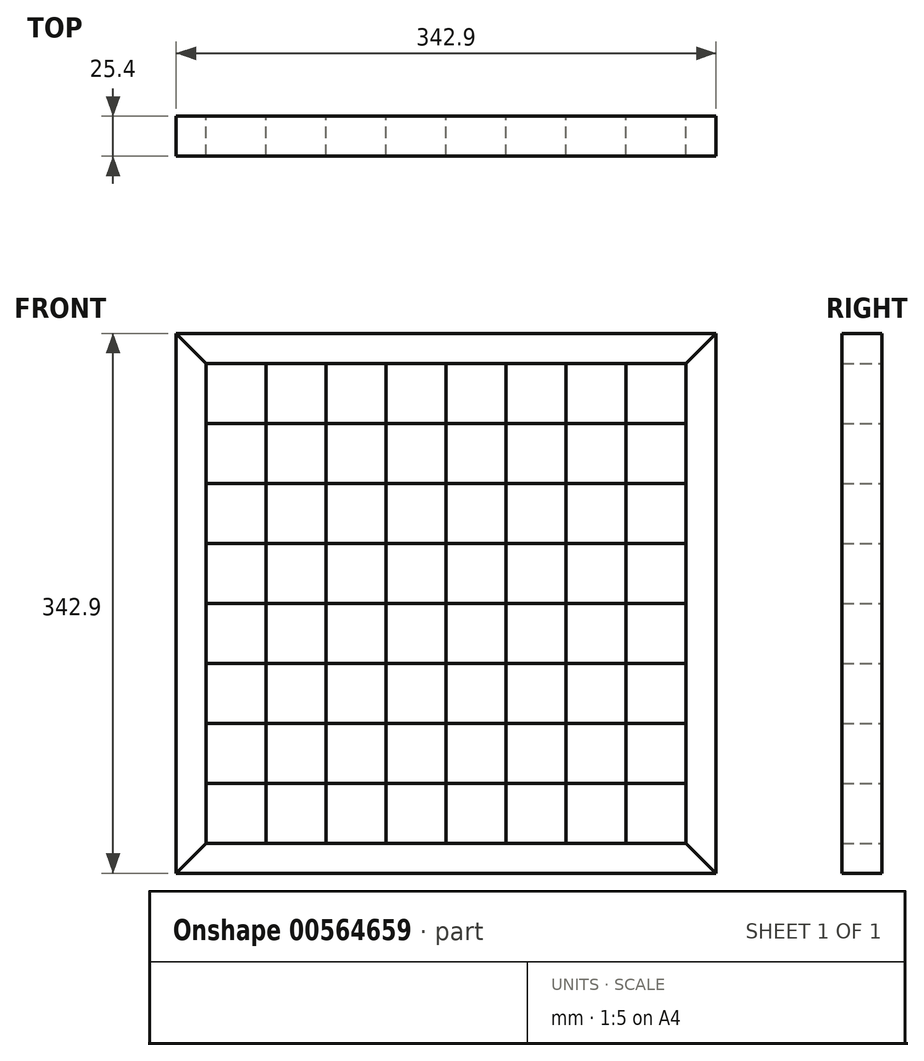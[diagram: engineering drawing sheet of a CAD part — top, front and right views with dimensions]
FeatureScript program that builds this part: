
annotation { "Feature Type Name" : "Feature", "Feature Type Description" : "" }
export const myFeature = defineFeature(function(context is Context, id is Id, definition is map)
    precondition{}
    {
        {
            var Q0;
            Q0=qCreatedBy(makeId("Front.planeOp"),FACE);
            var sketch = newSketch(context, id + "F0", { "sketchPlane" : qUnion([Q0])});
            skLineSegment(sketch, "E0.bottom", {"start": v(171.45, -171.45) * mm, "end": v(-171.45, -171.45) * mm});
            skLineSegment(sketch, "E0.top", {"start": v(171.45, 171.45) * mm, "end": v(-171.45, 171.45) * mm});
            skLineSegment(sketch, "E0.left", {"start": v(171.45, -171.45) * mm, "end": v(171.45, 171.45) * mm});
            skLineSegment(sketch, "E0.right", {"start": v(-171.45, -171.45) * mm, "end": v(-171.45, 171.45) * mm});
            skPoint(sketch, "E0.middle", {"position": v(0, 0) * mm});
            skLineSegment(sketch, "E1.bottom", {"start": v(152.4, -152.4) * mm, "end": v(-152.4, -152.4) * mm});
            skLineSegment(sketch, "E1.top", {"start": v(152.4, 152.4) * mm, "end": v(-152.4, 152.4) * mm});
            skLineSegment(sketch, "E1.left", {"start": v(152.4, -152.4) * mm, "end": v(152.4, 152.4) * mm});
            skLineSegment(sketch, "E1.right", {"start": v(-152.4, -152.4) * mm, "end": v(-152.4, 152.4) * mm});
            skLineSegment(sketch, "E2.0", {"start": v(152.4, 114.3) * mm, "end": v(-152.4, 114.3) * mm});
            skLineSegment(sketch, "E3.0", {"start": v(152.4, 76.2) * mm, "end": v(-152.4, 76.2) * mm});
            skLineSegment(sketch, "E4.0", {"start": v(152.4, 38.1) * mm, "end": v(-152.4, 38.1) * mm});
            skLineSegment(sketch, "E5.0", {"start": v(152.4, 0) * mm, "end": v(-152.4, 0) * mm});
            skLineSegment(sketch, "E6.0", {"start": v(152.4, -38.1) * mm, "end": v(-152.4, -38.1) * mm});
            skLineSegment(sketch, "E7.0", {"start": v(152.4, -76.2) * mm, "end": v(-152.4, -76.2) * mm});
            skLineSegment(sketch, "E8.0", {"start": v(152.4, -114.3) * mm, "end": v(-152.4, -114.3) * mm});
            skLineSegment(sketch, "E9.0", {"start": v(-114.3, -152.4) * mm, "end": v(-114.3, 152.4) * mm});
            skLineSegment(sketch, "E10.0", {"start": v(-76.2, -152.4) * mm, "end": v(-76.2, 152.4) * mm});
            skLineSegment(sketch, "E11.0", {"start": v(-38.1, -152.4) * mm, "end": v(-38.1, 152.4) * mm});
            skLineSegment(sketch, "E12.0", {"start": v(0, -152.4) * mm, "end": v(0, 152.4) * mm});
            skLineSegment(sketch, "E13.0", {"start": v(38.1, -152.4) * mm, "end": v(38.1, 152.4) * mm});
            skLineSegment(sketch, "E14.0", {"start": v(76.2, -152.4) * mm, "end": v(76.2, 152.4) * mm});
            skLineSegment(sketch, "E15.0", {"start": v(114.3, -152.4) * mm, "end": v(114.3, 152.4) * mm});
            skLineSegment(sketch, "E16", {"start": v(-152.4, 152.4) * mm, "end": v(-171.45, 171.45) * mm});
            skLineSegment(sketch, "E17", {"start": v(171.45, 171.45) * mm, "end": v(152.4, 152.4) * mm});
            skLineSegment(sketch, "E18", {"start": v(152.4, -152.4) * mm, "end": v(171.45, -171.45) * mm});
            skLineSegment(sketch, "E19", {"start": v(-152.4, -152.4) * mm, "end": v(-171.45, -171.45) * mm});
            skSolve(sketch);
        }
        {
            var Q0;
            Q0=makeQuery(id+"F0.imprint","IMPRINT",FACE,{"disambiguationData":[TD([[makeQuery(id+"F0.imprint","IMPRINT",EDGE,{"derivedFrom":sQuery(id+"F0.wireOp",EDGE,"E0.top")}),1.0]])]});
            extrude(context, id + "F1", {"entities" : qUnion([Q0]), "depth" : 25.4 * mm, "offsetDistance" : 25.4 * mm});
        }
        {
            var Q0;
            Q0=makeQuery(id+"F0.imprint","IMPRINT",FACE,{"disambiguationData":[TD([[makeQuery(id+"F0.imprint","IMPRINT",EDGE,{"derivedFrom":sQuery(id+"F0.wireOp",EDGE,"E0.right")}),-1.0]])]});
            extrude(context, id + "F2", {"entities" : qUnion([Q0]), "depth" : 25.4 * mm, "offsetDistance" : 25.4 * mm});
        }
        {
            var Q0;
            Q0=makeQuery(id+"F0.imprint","IMPRINT",FACE,{"disambiguationData":[TD([[makeQuery(id+"F0.imprint","IMPRINT",EDGE,{"derivedFrom":sQuery(id+"F0.wireOp",EDGE,"E0.left")}),1.0]])]});
            extrude(context, id + "F3", {"entities" : qUnion([Q0]), "depth" : 25.4 * mm, "offsetDistance" : 25.4 * mm});
        }
        {
            var Q0;
            Q0=makeQuery(id+"F0.imprint","IMPRINT",FACE,{"disambiguationData":[TD([[makeQuery(id+"F0.imprint","IMPRINT",EDGE,{"derivedFrom":sQuery(id+"F0.wireOp",EDGE,"E0.bottom")}),-1.0]])]});
            extrude(context, id + "F4", {"entities" : qUnion([Q0]), "depth" : 25.4 * mm, "offsetDistance" : 25.4 * mm});
        }
        {
            var Q0;
            {var subQ0=sQuery(id+"F0.wireOp",EDGE,"E1.right");var subQ5=sQuery(id+"F0.wireOp",EDGE,"E2.0");var subQ7=makeQuery(id+"F0.imprint","INTERSECT",VERTEX,{"derivedFrom":[subQ0,subQ5]});Q0=makeQuery(id+"F0.imprint","IMPRINT",FACE,{"disambiguationData":[TD([[makeQuery(id+"F0.imprint","IMPRINT",EDGE,{"disambiguationData":[TD([[subQ7,1.0]])],"derivedFrom":subQ5}),-1.0]])]});}
            extrude(context, id + "F5", {"entities" : qUnion([Q0]), "depth" : 25.4 * mm, "offsetDistance" : 25.4 * mm});
        }
        {
            var Q0;
            {var subQ0=sQuery(id+"F0.wireOp",EDGE,"E2.0");var subQ1=sQuery(id+"F0.wireOp",EDGE,"E1.right");var subQ2=makeQuery(id+"F0.imprint","INTERSECT",VERTEX,{"derivedFrom":[subQ1,subQ0]});Q0=makeQuery(id+"F0.imprint","IMPRINT",FACE,{"disambiguationData":[TD([[makeQuery(id+"F0.imprint","IMPRINT",EDGE,{"disambiguationData":[TD([[subQ2,1.0]])],"derivedFrom":subQ1}),-1.0]])]});}
            extrude(context, id + "F6", {"entities" : qUnion([Q0]), "depth" : 25.4 * mm, "offsetDistance" : 25.4 * mm});
        }
        {
            var Q0;
            {var subQ0=sQuery(id+"F0.wireOp",EDGE,"E3.0");var subQ1=sQuery(id+"F0.wireOp",EDGE,"E1.right");var subQ2=makeQuery(id+"F0.imprint","INTERSECT",VERTEX,{"derivedFrom":[subQ1,subQ0]});Q0=makeQuery(id+"F0.imprint","IMPRINT",FACE,{"disambiguationData":[TD([[makeQuery(id+"F0.imprint","IMPRINT",EDGE,{"disambiguationData":[TD([[subQ2,1.0]])],"derivedFrom":subQ1}),-1.0]])]});}
            extrude(context, id + "F7", {"entities" : qUnion([Q0]), "depth" : 25.4 * mm, "offsetDistance" : 25.4 * mm});
        }
        {
            var Q0;
            {var subQ0=sQuery(id+"F0.wireOp",EDGE,"E4.0");var subQ1=sQuery(id+"F0.wireOp",EDGE,"E1.right");var subQ2=makeQuery(id+"F0.imprint","INTERSECT",VERTEX,{"derivedFrom":[subQ1,subQ0]});Q0=makeQuery(id+"F0.imprint","IMPRINT",FACE,{"disambiguationData":[TD([[makeQuery(id+"F0.imprint","IMPRINT",EDGE,{"disambiguationData":[TD([[subQ2,1.0]])],"derivedFrom":subQ1}),-1.0]])]});}
            extrude(context, id + "F8", {"entities" : qUnion([Q0]), "depth" : 25.4 * mm, "offsetDistance" : 25.4 * mm});
        }
        {
            var Q0;
            {var subQ0=sQuery(id+"F0.wireOp",EDGE,"E5.0");var subQ1=sQuery(id+"F0.wireOp",EDGE,"E1.right");var subQ2=makeQuery(id+"F0.imprint","INTERSECT",VERTEX,{"derivedFrom":[subQ1,subQ0]});Q0=makeQuery(id+"F0.imprint","IMPRINT",FACE,{"disambiguationData":[TD([[makeQuery(id+"F0.imprint","IMPRINT",EDGE,{"disambiguationData":[TD([[subQ2,1.0]])],"derivedFrom":subQ1}),-1.0]])]});}
            extrude(context, id + "F9", {"entities" : qUnion([Q0]), "depth" : 25.4 * mm, "offsetDistance" : 25.4 * mm});
        }
        {
            var Q0;
            {var subQ0=sQuery(id+"F0.wireOp",EDGE,"E6.0");var subQ1=sQuery(id+"F0.wireOp",EDGE,"E1.right");var subQ2=makeQuery(id+"F0.imprint","INTERSECT",VERTEX,{"derivedFrom":[subQ1,subQ0]});Q0=makeQuery(id+"F0.imprint","IMPRINT",FACE,{"disambiguationData":[TD([[makeQuery(id+"F0.imprint","IMPRINT",EDGE,{"disambiguationData":[TD([[subQ2,1.0]])],"derivedFrom":subQ1}),-1.0]])]});}
            extrude(context, id + "F10", {"entities" : qUnion([Q0]), "depth" : 25.4 * mm, "offsetDistance" : 25.4 * mm});
        }
        {
            var Q0;
            {var subQ0=sQuery(id+"F0.wireOp",EDGE,"E7.0");var subQ1=sQuery(id+"F0.wireOp",EDGE,"E1.right");var subQ2=makeQuery(id+"F0.imprint","INTERSECT",VERTEX,{"derivedFrom":[subQ1,subQ0]});Q0=makeQuery(id+"F0.imprint","IMPRINT",FACE,{"disambiguationData":[TD([[makeQuery(id+"F0.imprint","IMPRINT",EDGE,{"disambiguationData":[TD([[subQ2,1.0]])],"derivedFrom":subQ1}),-1.0]])]});}
            extrude(context, id + "F11", {"entities" : qUnion([Q0]), "depth" : 25.4 * mm, "offsetDistance" : 25.4 * mm});
        }
        {
            var Q0;
            {var subQ0=sQuery(id+"F0.wireOp",EDGE,"E1.right");var subQ5=sQuery(id+"F0.wireOp",EDGE,"E8.0");var subQ6=makeQuery(id+"F0.imprint","INTERSECT",VERTEX,{"derivedFrom":[subQ0,subQ5]});Q0=makeQuery(id+"F0.imprint","IMPRINT",FACE,{"disambiguationData":[TD([[makeQuery(id+"F0.imprint","IMPRINT",EDGE,{"disambiguationData":[TD([[subQ6,1.0]])],"derivedFrom":subQ5}),1.0]])]});}
            extrude(context, id + "F12", {"entities" : qUnion([Q0]), "depth" : 25.4 * mm, "offsetDistance" : 25.4 * mm});
        }
        {
            var Q0;
            {var subQ0=sQuery(id+"F0.wireOp",EDGE,"E9.0");var subQ1=sQuery(id+"F0.wireOp",EDGE,"E1.top");var subQ2=makeQuery(id+"F0.imprint","INTERSECT",VERTEX,{"derivedFrom":[subQ1,subQ0]});Q0=makeQuery(id+"F0.imprint","IMPRINT",FACE,{"disambiguationData":[TD([[makeQuery(id+"F0.imprint","IMPRINT",EDGE,{"disambiguationData":[TD([[subQ2,1.0]])],"derivedFrom":subQ1}),1.0]])]});}
            extrude(context, id + "F13", {"entities" : qUnion([Q0]), "depth" : 25.4 * mm, "offsetDistance" : 25.4 * mm});
        }
        {
            var Q0;
            {var subQ0=sQuery(id+"F0.wireOp",EDGE,"E10.0");var subQ1=sQuery(id+"F0.wireOp",EDGE,"E1.top");var subQ2=makeQuery(id+"F0.imprint","INTERSECT",VERTEX,{"derivedFrom":[subQ1,subQ0]});Q0=makeQuery(id+"F0.imprint","IMPRINT",FACE,{"disambiguationData":[TD([[makeQuery(id+"F0.imprint","IMPRINT",EDGE,{"disambiguationData":[TD([[subQ2,1.0]])],"derivedFrom":subQ1}),1.0]])]});}
            extrude(context, id + "F14", {"entities" : qUnion([Q0]), "depth" : 25.4 * mm, "offsetDistance" : 25.4 * mm});
        }
        {
            var Q0;
            {var subQ0=sQuery(id+"F0.wireOp",EDGE,"E11.0");var subQ1=sQuery(id+"F0.wireOp",EDGE,"E1.top");var subQ2=makeQuery(id+"F0.imprint","INTERSECT",VERTEX,{"derivedFrom":[subQ1,subQ0]});Q0=makeQuery(id+"F0.imprint","IMPRINT",FACE,{"disambiguationData":[TD([[makeQuery(id+"F0.imprint","IMPRINT",EDGE,{"disambiguationData":[TD([[subQ2,1.0]])],"derivedFrom":subQ1}),1.0]])]});}
            extrude(context, id + "F15", {"entities" : qUnion([Q0]), "depth" : 25.4 * mm, "offsetDistance" : 25.4 * mm});
        }
        {
            var Q0;
            {var subQ0=sQuery(id+"F0.wireOp",EDGE,"E12.0");var subQ1=sQuery(id+"F0.wireOp",EDGE,"E1.top");var subQ2=makeQuery(id+"F0.imprint","INTERSECT",VERTEX,{"derivedFrom":[subQ1,subQ0]});Q0=makeQuery(id+"F0.imprint","IMPRINT",FACE,{"disambiguationData":[TD([[makeQuery(id+"F0.imprint","IMPRINT",EDGE,{"disambiguationData":[TD([[subQ2,1.0]])],"derivedFrom":subQ1}),1.0]])]});}
            extrude(context, id + "F16", {"entities" : qUnion([Q0]), "depth" : 25.4 * mm, "offsetDistance" : 25.4 * mm});
        }
        {
            var Q0;
            {var subQ0=sQuery(id+"F0.wireOp",EDGE,"E13.0");var subQ1=sQuery(id+"F0.wireOp",EDGE,"E1.top");var subQ2=makeQuery(id+"F0.imprint","INTERSECT",VERTEX,{"derivedFrom":[subQ1,subQ0]});Q0=makeQuery(id+"F0.imprint","IMPRINT",FACE,{"disambiguationData":[TD([[makeQuery(id+"F0.imprint","IMPRINT",EDGE,{"disambiguationData":[TD([[subQ2,1.0]])],"derivedFrom":subQ1}),1.0]])]});}
            extrude(context, id + "F17", {"entities" : qUnion([Q0]), "depth" : 25.4 * mm, "offsetDistance" : 25.4 * mm});
        }
        {
            var Q0;
            {var subQ0=sQuery(id+"F0.wireOp",EDGE,"E14.0");var subQ1=sQuery(id+"F0.wireOp",EDGE,"E1.top");var subQ2=makeQuery(id+"F0.imprint","INTERSECT",VERTEX,{"derivedFrom":[subQ1,subQ0]});Q0=makeQuery(id+"F0.imprint","IMPRINT",FACE,{"disambiguationData":[TD([[makeQuery(id+"F0.imprint","IMPRINT",EDGE,{"disambiguationData":[TD([[subQ2,1.0]])],"derivedFrom":subQ1}),1.0]])]});}
            extrude(context, id + "F18", {"entities" : qUnion([Q0]), "depth" : 25.4 * mm, "offsetDistance" : 25.4 * mm});
        }
        {
            var Q0;
            {var subQ0=sQuery(id+"F0.wireOp",EDGE,"E1.left");var subQ5=sQuery(id+"F0.wireOp",EDGE,"E2.0");var subQ6=makeQuery(id+"F0.imprint","INTERSECT",VERTEX,{"derivedFrom":[subQ0,subQ5]});Q0=makeQuery(id+"F0.imprint","IMPRINT",FACE,{"disambiguationData":[TD([[makeQuery(id+"F0.imprint","IMPRINT",EDGE,{"disambiguationData":[TD([[subQ6,-1.0]])],"derivedFrom":subQ5}),-1.0]])]});}
            extrude(context, id + "F19", {"entities" : qUnion([Q0]), "depth" : 25.4 * mm, "offsetDistance" : 25.4 * mm});
        }
        {
            var Q0;
            {var subQ0=sQuery(id+"F0.wireOp",EDGE,"E10.0");var subQ1=sQuery(id+"F0.wireOp",EDGE,"E2.0");var subQ2=makeQuery(id+"F0.imprint","INTERSECT",VERTEX,{"derivedFrom":[subQ1,subQ0]});Q0=makeQuery(id+"F0.imprint","IMPRINT",FACE,{"disambiguationData":[TD([[makeQuery(id+"F0.imprint","IMPRINT",EDGE,{"disambiguationData":[TD([[subQ2,-1.0]])],"derivedFrom":subQ1}),1.0]])]});}
            var Q1;
            {var subQ0=sQuery(id+"F0.wireOp",EDGE,"E11.0");var subQ1=sQuery(id+"F0.wireOp",EDGE,"E3.0");var subQ2=makeQuery(id+"F0.imprint","INTERSECT",VERTEX,{"derivedFrom":[subQ1,subQ0]});Q1=makeQuery(id+"F0.imprint","IMPRINT",FACE,{"disambiguationData":[TD([[makeQuery(id+"F0.imprint","IMPRINT",EDGE,{"disambiguationData":[TD([[subQ2,-1.0]])],"derivedFrom":subQ1}),1.0]])]});}
            var Q2;
            {var subQ0=sQuery(id+"F0.wireOp",EDGE,"E12.0");var subQ1=sQuery(id+"F0.wireOp",EDGE,"E4.0");var subQ2=makeQuery(id+"F0.imprint","INTERSECT",VERTEX,{"derivedFrom":[subQ1,subQ0]});Q2=makeQuery(id+"F0.imprint","IMPRINT",FACE,{"disambiguationData":[TD([[makeQuery(id+"F0.imprint","IMPRINT",EDGE,{"disambiguationData":[TD([[subQ2,-1.0]])],"derivedFrom":subQ1}),1.0]])]});}
            var Q3;
            {var subQ0=sQuery(id+"F0.wireOp",EDGE,"E13.0");var subQ1=sQuery(id+"F0.wireOp",EDGE,"E5.0");var subQ2=makeQuery(id+"F0.imprint","INTERSECT",VERTEX,{"derivedFrom":[subQ1,subQ0]});Q3=makeQuery(id+"F0.imprint","IMPRINT",FACE,{"disambiguationData":[TD([[makeQuery(id+"F0.imprint","IMPRINT",EDGE,{"disambiguationData":[TD([[subQ2,-1.0]])],"derivedFrom":subQ1}),1.0]])]});}
            extrude(context, id + "F20", {"entities" : qUnion([Q0, Q1, Q2, Q3]), "depth" : 25.4 * mm, "offsetDistance" : 25.4 * mm});
        }
        {
            var Q0;
            {var subQ0=sQuery(id+"F0.wireOp",EDGE,"E14.0");var subQ1=sQuery(id+"F0.wireOp",EDGE,"E6.0");var subQ2=makeQuery(id+"F0.imprint","INTERSECT",VERTEX,{"derivedFrom":[subQ1,subQ0]});Q0=makeQuery(id+"F0.imprint","IMPRINT",FACE,{"disambiguationData":[TD([[makeQuery(id+"F0.imprint","IMPRINT",EDGE,{"disambiguationData":[TD([[subQ2,-1.0]])],"derivedFrom":subQ1}),1.0]])]});}
            var Q1;
            {var subQ0=sQuery(id+"F0.wireOp",EDGE,"E15.0");var subQ1=sQuery(id+"F0.wireOp",EDGE,"E7.0");var subQ2=makeQuery(id+"F0.imprint","INTERSECT",VERTEX,{"derivedFrom":[subQ1,subQ0]});Q1=makeQuery(id+"F0.imprint","IMPRINT",FACE,{"disambiguationData":[TD([[makeQuery(id+"F0.imprint","IMPRINT",EDGE,{"disambiguationData":[TD([[subQ2,-1.0]])],"derivedFrom":subQ1}),1.0]])]});}
            var Q2;
            {var subQ0=sQuery(id+"F0.wireOp",EDGE,"E1.left");var subQ5=sQuery(id+"F0.wireOp",EDGE,"E8.0");var subQ6=makeQuery(id+"F0.imprint","INTERSECT",VERTEX,{"derivedFrom":[subQ0,subQ5]});Q2=makeQuery(id+"F0.imprint","IMPRINT",FACE,{"disambiguationData":[TD([[makeQuery(id+"F0.imprint","IMPRINT",EDGE,{"disambiguationData":[TD([[subQ6,-1.0]])],"derivedFrom":subQ5}),1.0]])]});}
            extrude(context, id + "F21", {"entities" : qUnion([Q0, Q1, Q2]), "depth" : 25.4 * mm, "offsetDistance" : 25.4 * mm});
        }
        {
            var Q0;
            {var subQ0=sQuery(id+"F0.wireOp",EDGE,"E10.0");var subQ1=sQuery(id+"F0.wireOp",EDGE,"E3.0");var subQ2=makeQuery(id+"F0.imprint","INTERSECT",VERTEX,{"derivedFrom":[subQ1,subQ0]});Q0=makeQuery(id+"F0.imprint","IMPRINT",FACE,{"disambiguationData":[TD([[makeQuery(id+"F0.imprint","IMPRINT",EDGE,{"disambiguationData":[TD([[subQ2,-1.0]])],"derivedFrom":subQ1}),1.0]])]});}
            var Q1;
            {var subQ0=sQuery(id+"F0.wireOp",EDGE,"E11.0");var subQ1=sQuery(id+"F0.wireOp",EDGE,"E4.0");var subQ2=makeQuery(id+"F0.imprint","INTERSECT",VERTEX,{"derivedFrom":[subQ1,subQ0]});Q1=makeQuery(id+"F0.imprint","IMPRINT",FACE,{"disambiguationData":[TD([[makeQuery(id+"F0.imprint","IMPRINT",EDGE,{"disambiguationData":[TD([[subQ2,-1.0]])],"derivedFrom":subQ1}),1.0]])]});}
            var Q2;
            {var subQ0=sQuery(id+"F0.wireOp",EDGE,"E12.0");var subQ1=sQuery(id+"F0.wireOp",EDGE,"E5.0");var subQ2=makeQuery(id+"F0.imprint","INTERSECT",VERTEX,{"derivedFrom":[subQ1,subQ0]});Q2=makeQuery(id+"F0.imprint","IMPRINT",FACE,{"disambiguationData":[TD([[makeQuery(id+"F0.imprint","IMPRINT",EDGE,{"disambiguationData":[TD([[subQ2,-1.0]])],"derivedFrom":subQ1}),1.0]])]});}
            var Q3;
            {var subQ0=sQuery(id+"F0.wireOp",EDGE,"E13.0");var subQ1=sQuery(id+"F0.wireOp",EDGE,"E6.0");var subQ2=makeQuery(id+"F0.imprint","INTERSECT",VERTEX,{"derivedFrom":[subQ1,subQ0]});Q3=makeQuery(id+"F0.imprint","IMPRINT",FACE,{"disambiguationData":[TD([[makeQuery(id+"F0.imprint","IMPRINT",EDGE,{"disambiguationData":[TD([[subQ2,-1.0]])],"derivedFrom":subQ1}),1.0]])]});}
            var Q4;
            {var subQ0=sQuery(id+"F0.wireOp",EDGE,"E14.0");var subQ1=sQuery(id+"F0.wireOp",EDGE,"E7.0");var subQ2=makeQuery(id+"F0.imprint","INTERSECT",VERTEX,{"derivedFrom":[subQ1,subQ0]});Q4=makeQuery(id+"F0.imprint","IMPRINT",FACE,{"disambiguationData":[TD([[makeQuery(id+"F0.imprint","IMPRINT",EDGE,{"disambiguationData":[TD([[subQ2,-1.0]])],"derivedFrom":subQ1}),1.0]])]});}
            var Q5;
            {var subQ0=sQuery(id+"F0.wireOp",EDGE,"E14.0");var subQ1=sQuery(id+"F0.wireOp",EDGE,"E1.bottom");var subQ2=makeQuery(id+"F0.imprint","INTERSECT",VERTEX,{"derivedFrom":[subQ1,subQ0]});Q5=makeQuery(id+"F0.imprint","IMPRINT",FACE,{"disambiguationData":[TD([[makeQuery(id+"F0.imprint","IMPRINT",EDGE,{"disambiguationData":[TD([[subQ2,1.0]])],"derivedFrom":subQ1}),-1.0]])]});}
            extrude(context, id + "F22", {"entities" : qUnion([Q0, Q1, Q2, Q3, Q4, Q5]), "depth" : 25.4 * mm, "offsetDistance" : 25.4 * mm});
        }
        {
            var Q0;
            {var subQ0=sQuery(id+"F0.wireOp",EDGE,"E10.0");var subQ1=sQuery(id+"F0.wireOp",EDGE,"E4.0");var subQ2=makeQuery(id+"F0.imprint","INTERSECT",VERTEX,{"derivedFrom":[subQ1,subQ0]});Q0=makeQuery(id+"F0.imprint","IMPRINT",FACE,{"disambiguationData":[TD([[makeQuery(id+"F0.imprint","IMPRINT",EDGE,{"disambiguationData":[TD([[subQ2,-1.0]])],"derivedFrom":subQ1}),1.0]])]});}
            var Q1;
            {var subQ0=sQuery(id+"F0.wireOp",EDGE,"E11.0");var subQ1=sQuery(id+"F0.wireOp",EDGE,"E5.0");var subQ2=makeQuery(id+"F0.imprint","INTERSECT",VERTEX,{"derivedFrom":[subQ1,subQ0]});Q1=makeQuery(id+"F0.imprint","IMPRINT",FACE,{"disambiguationData":[TD([[makeQuery(id+"F0.imprint","IMPRINT",EDGE,{"disambiguationData":[TD([[subQ2,-1.0]])],"derivedFrom":subQ1}),1.0]])]});}
            var Q2;
            {var subQ0=sQuery(id+"F0.wireOp",EDGE,"E12.0");var subQ1=sQuery(id+"F0.wireOp",EDGE,"E6.0");var subQ2=makeQuery(id+"F0.imprint","INTERSECT",VERTEX,{"derivedFrom":[subQ1,subQ0]});Q2=makeQuery(id+"F0.imprint","IMPRINT",FACE,{"disambiguationData":[TD([[makeQuery(id+"F0.imprint","IMPRINT",EDGE,{"disambiguationData":[TD([[subQ2,-1.0]])],"derivedFrom":subQ1}),1.0]])]});}
            var Q3;
            {var subQ0=sQuery(id+"F0.wireOp",EDGE,"E13.0");var subQ1=sQuery(id+"F0.wireOp",EDGE,"E7.0");var subQ2=makeQuery(id+"F0.imprint","INTERSECT",VERTEX,{"derivedFrom":[subQ1,subQ0]});Q3=makeQuery(id+"F0.imprint","IMPRINT",FACE,{"disambiguationData":[TD([[makeQuery(id+"F0.imprint","IMPRINT",EDGE,{"disambiguationData":[TD([[subQ2,-1.0]])],"derivedFrom":subQ1}),1.0]])]});}
            var Q4;
            {var subQ0=sQuery(id+"F0.wireOp",EDGE,"E13.0");var subQ1=sQuery(id+"F0.wireOp",EDGE,"E1.bottom");var subQ2=makeQuery(id+"F0.imprint","INTERSECT",VERTEX,{"derivedFrom":[subQ1,subQ0]});Q4=makeQuery(id+"F0.imprint","IMPRINT",FACE,{"disambiguationData":[TD([[makeQuery(id+"F0.imprint","IMPRINT",EDGE,{"disambiguationData":[TD([[subQ2,1.0]])],"derivedFrom":subQ1}),-1.0]])]});}
            extrude(context, id + "F23", {"entities" : qUnion([Q0, Q1, Q2, Q3, Q4]), "depth" : 25.4 * mm, "offsetDistance" : 25.4 * mm});
        }
        {
            var Q0;
            {var subQ0=sQuery(id+"F0.wireOp",EDGE,"E10.0");var subQ1=sQuery(id+"F0.wireOp",EDGE,"E5.0");var subQ2=makeQuery(id+"F0.imprint","INTERSECT",VERTEX,{"derivedFrom":[subQ1,subQ0]});Q0=makeQuery(id+"F0.imprint","IMPRINT",FACE,{"disambiguationData":[TD([[makeQuery(id+"F0.imprint","IMPRINT",EDGE,{"disambiguationData":[TD([[subQ2,-1.0]])],"derivedFrom":subQ1}),1.0]])]});}
            var Q1;
            {var subQ0=sQuery(id+"F0.wireOp",EDGE,"E11.0");var subQ1=sQuery(id+"F0.wireOp",EDGE,"E6.0");var subQ2=makeQuery(id+"F0.imprint","INTERSECT",VERTEX,{"derivedFrom":[subQ1,subQ0]});Q1=makeQuery(id+"F0.imprint","IMPRINT",FACE,{"disambiguationData":[TD([[makeQuery(id+"F0.imprint","IMPRINT",EDGE,{"disambiguationData":[TD([[subQ2,-1.0]])],"derivedFrom":subQ1}),1.0]])]});}
            var Q2;
            {var subQ0=sQuery(id+"F0.wireOp",EDGE,"E12.0");var subQ1=sQuery(id+"F0.wireOp",EDGE,"E7.0");var subQ2=makeQuery(id+"F0.imprint","INTERSECT",VERTEX,{"derivedFrom":[subQ1,subQ0]});Q2=makeQuery(id+"F0.imprint","IMPRINT",FACE,{"disambiguationData":[TD([[makeQuery(id+"F0.imprint","IMPRINT",EDGE,{"disambiguationData":[TD([[subQ2,-1.0]])],"derivedFrom":subQ1}),1.0]])]});}
            var Q3;
            {var subQ0=sQuery(id+"F0.wireOp",EDGE,"E12.0");var subQ1=sQuery(id+"F0.wireOp",EDGE,"E1.bottom");var subQ2=makeQuery(id+"F0.imprint","INTERSECT",VERTEX,{"derivedFrom":[subQ1,subQ0]});Q3=makeQuery(id+"F0.imprint","IMPRINT",FACE,{"disambiguationData":[TD([[makeQuery(id+"F0.imprint","IMPRINT",EDGE,{"disambiguationData":[TD([[subQ2,1.0]])],"derivedFrom":subQ1}),-1.0]])]});}
            extrude(context, id + "F24", {"entities" : qUnion([Q0, Q1, Q2, Q3]), "depth" : 25.4 * mm, "offsetDistance" : 25.4 * mm});
        }
        {
            var Q0;
            {var subQ0=sQuery(id+"F0.wireOp",EDGE,"E10.0");var subQ1=sQuery(id+"F0.wireOp",EDGE,"E6.0");var subQ2=makeQuery(id+"F0.imprint","INTERSECT",VERTEX,{"derivedFrom":[subQ1,subQ0]});Q0=makeQuery(id+"F0.imprint","IMPRINT",FACE,{"disambiguationData":[TD([[makeQuery(id+"F0.imprint","IMPRINT",EDGE,{"disambiguationData":[TD([[subQ2,-1.0]])],"derivedFrom":subQ1}),1.0]])]});}
            var Q1;
            {var subQ0=sQuery(id+"F0.wireOp",EDGE,"E11.0");var subQ1=sQuery(id+"F0.wireOp",EDGE,"E7.0");var subQ2=makeQuery(id+"F0.imprint","INTERSECT",VERTEX,{"derivedFrom":[subQ1,subQ0]});Q1=makeQuery(id+"F0.imprint","IMPRINT",FACE,{"disambiguationData":[TD([[makeQuery(id+"F0.imprint","IMPRINT",EDGE,{"disambiguationData":[TD([[subQ2,-1.0]])],"derivedFrom":subQ1}),1.0]])]});}
            var Q2;
            {var subQ0=sQuery(id+"F0.wireOp",EDGE,"E11.0");var subQ1=sQuery(id+"F0.wireOp",EDGE,"E1.bottom");var subQ2=makeQuery(id+"F0.imprint","INTERSECT",VERTEX,{"derivedFrom":[subQ1,subQ0]});Q2=makeQuery(id+"F0.imprint","IMPRINT",FACE,{"disambiguationData":[TD([[makeQuery(id+"F0.imprint","IMPRINT",EDGE,{"disambiguationData":[TD([[subQ2,1.0]])],"derivedFrom":subQ1}),-1.0]])]});}
            extrude(context, id + "F25", {"entities" : qUnion([Q0, Q1, Q2]), "depth" : 25.4 * mm, "offsetDistance" : 25.4 * mm});
        }
        {
            var Q0;
            {var subQ0=sQuery(id+"F0.wireOp",EDGE,"E10.0");var subQ1=sQuery(id+"F0.wireOp",EDGE,"E7.0");var subQ2=makeQuery(id+"F0.imprint","INTERSECT",VERTEX,{"derivedFrom":[subQ1,subQ0]});Q0=makeQuery(id+"F0.imprint","IMPRINT",FACE,{"disambiguationData":[TD([[makeQuery(id+"F0.imprint","IMPRINT",EDGE,{"disambiguationData":[TD([[subQ2,-1.0]])],"derivedFrom":subQ1}),1.0]])]});}
            var Q1;
            {var subQ0=sQuery(id+"F0.wireOp",EDGE,"E10.0");var subQ1=sQuery(id+"F0.wireOp",EDGE,"E1.bottom");var subQ2=makeQuery(id+"F0.imprint","INTERSECT",VERTEX,{"derivedFrom":[subQ1,subQ0]});Q1=makeQuery(id+"F0.imprint","IMPRINT",FACE,{"disambiguationData":[TD([[makeQuery(id+"F0.imprint","IMPRINT",EDGE,{"disambiguationData":[TD([[subQ2,1.0]])],"derivedFrom":subQ1}),-1.0]])]});}
            extrude(context, id + "F26", {"entities" : qUnion([Q0, Q1]), "depth" : 25.4 * mm, "offsetDistance" : 25.4 * mm});
        }
        {
            var Q0;
            {var subQ0=sQuery(id+"F0.wireOp",EDGE,"E9.0");var subQ1=sQuery(id+"F0.wireOp",EDGE,"E1.bottom");var subQ2=makeQuery(id+"F0.imprint","INTERSECT",VERTEX,{"derivedFrom":[subQ1,subQ0]});Q0=makeQuery(id+"F0.imprint","IMPRINT",FACE,{"disambiguationData":[TD([[makeQuery(id+"F0.imprint","IMPRINT",EDGE,{"disambiguationData":[TD([[subQ2,1.0]])],"derivedFrom":subQ1}),-1.0]])]});}
            extrude(context, id + "F27", {"entities" : qUnion([Q0]), "depth" : 25.4 * mm, "offsetDistance" : 25.4 * mm});
        }
        {
            var Q0;
            {var subQ0=sQuery(id+"F0.wireOp",EDGE,"E11.0");var subQ1=sQuery(id+"F0.wireOp",EDGE,"E2.0");var subQ2=makeQuery(id+"F0.imprint","INTERSECT",VERTEX,{"derivedFrom":[subQ1,subQ0]});Q0=makeQuery(id+"F0.imprint","IMPRINT",FACE,{"disambiguationData":[TD([[makeQuery(id+"F0.imprint","IMPRINT",EDGE,{"disambiguationData":[TD([[subQ2,-1.0]])],"derivedFrom":subQ1}),1.0]])]});}
            var Q1;
            {var subQ0=sQuery(id+"F0.wireOp",EDGE,"E12.0");var subQ1=sQuery(id+"F0.wireOp",EDGE,"E3.0");var subQ2=makeQuery(id+"F0.imprint","INTERSECT",VERTEX,{"derivedFrom":[subQ1,subQ0]});Q1=makeQuery(id+"F0.imprint","IMPRINT",FACE,{"disambiguationData":[TD([[makeQuery(id+"F0.imprint","IMPRINT",EDGE,{"disambiguationData":[TD([[subQ2,-1.0]])],"derivedFrom":subQ1}),1.0]])]});}
            var Q2;
            {var subQ0=sQuery(id+"F0.wireOp",EDGE,"E13.0");var subQ1=sQuery(id+"F0.wireOp",EDGE,"E4.0");var subQ2=makeQuery(id+"F0.imprint","INTERSECT",VERTEX,{"derivedFrom":[subQ1,subQ0]});Q2=makeQuery(id+"F0.imprint","IMPRINT",FACE,{"disambiguationData":[TD([[makeQuery(id+"F0.imprint","IMPRINT",EDGE,{"disambiguationData":[TD([[subQ2,-1.0]])],"derivedFrom":subQ1}),1.0]])]});}
            var Q3;
            {var subQ0=sQuery(id+"F0.wireOp",EDGE,"E14.0");var subQ1=sQuery(id+"F0.wireOp",EDGE,"E5.0");var subQ2=makeQuery(id+"F0.imprint","INTERSECT",VERTEX,{"derivedFrom":[subQ1,subQ0]});Q3=makeQuery(id+"F0.imprint","IMPRINT",FACE,{"disambiguationData":[TD([[makeQuery(id+"F0.imprint","IMPRINT",EDGE,{"disambiguationData":[TD([[subQ2,-1.0]])],"derivedFrom":subQ1}),1.0]])]});}
            var Q4;
            {var subQ0=sQuery(id+"F0.wireOp",EDGE,"E15.0");var subQ1=sQuery(id+"F0.wireOp",EDGE,"E6.0");var subQ2=makeQuery(id+"F0.imprint","INTERSECT",VERTEX,{"derivedFrom":[subQ1,subQ0]});Q4=makeQuery(id+"F0.imprint","IMPRINT",FACE,{"disambiguationData":[TD([[makeQuery(id+"F0.imprint","IMPRINT",EDGE,{"disambiguationData":[TD([[subQ2,-1.0]])],"derivedFrom":subQ1}),1.0]])]});}
            var Q5;
            {var subQ0=sQuery(id+"F0.wireOp",EDGE,"E7.0");var subQ1=sQuery(id+"F0.wireOp",EDGE,"E1.left");var subQ2=makeQuery(id+"F0.imprint","INTERSECT",VERTEX,{"derivedFrom":[subQ1,subQ0]});Q5=makeQuery(id+"F0.imprint","IMPRINT",FACE,{"disambiguationData":[TD([[makeQuery(id+"F0.imprint","IMPRINT",EDGE,{"disambiguationData":[TD([[subQ2,1.0]])],"derivedFrom":subQ1}),1.0]])]});}
            extrude(context, id + "F28", {"entities" : qUnion([Q0, Q1, Q2, Q3, Q4, Q5]), "depth" : 25.4 * mm, "offsetDistance" : 25.4 * mm});
        }
        {
            var Q0;
            {var subQ0=sQuery(id+"F0.wireOp",EDGE,"E12.0");var subQ1=sQuery(id+"F0.wireOp",EDGE,"E2.0");var subQ2=makeQuery(id+"F0.imprint","INTERSECT",VERTEX,{"derivedFrom":[subQ1,subQ0]});Q0=makeQuery(id+"F0.imprint","IMPRINT",FACE,{"disambiguationData":[TD([[makeQuery(id+"F0.imprint","IMPRINT",EDGE,{"disambiguationData":[TD([[subQ2,-1.0]])],"derivedFrom":subQ1}),1.0]])]});}
            var Q1;
            {var subQ0=sQuery(id+"F0.wireOp",EDGE,"E13.0");var subQ1=sQuery(id+"F0.wireOp",EDGE,"E3.0");var subQ2=makeQuery(id+"F0.imprint","INTERSECT",VERTEX,{"derivedFrom":[subQ1,subQ0]});Q1=makeQuery(id+"F0.imprint","IMPRINT",FACE,{"disambiguationData":[TD([[makeQuery(id+"F0.imprint","IMPRINT",EDGE,{"disambiguationData":[TD([[subQ2,-1.0]])],"derivedFrom":subQ1}),1.0]])]});}
            var Q2;
            {var subQ0=sQuery(id+"F0.wireOp",EDGE,"E14.0");var subQ1=sQuery(id+"F0.wireOp",EDGE,"E4.0");var subQ2=makeQuery(id+"F0.imprint","INTERSECT",VERTEX,{"derivedFrom":[subQ1,subQ0]});Q2=makeQuery(id+"F0.imprint","IMPRINT",FACE,{"disambiguationData":[TD([[makeQuery(id+"F0.imprint","IMPRINT",EDGE,{"disambiguationData":[TD([[subQ2,-1.0]])],"derivedFrom":subQ1}),1.0]])]});}
            var Q3;
            {var subQ0=sQuery(id+"F0.wireOp",EDGE,"E15.0");var subQ1=sQuery(id+"F0.wireOp",EDGE,"E5.0");var subQ2=makeQuery(id+"F0.imprint","INTERSECT",VERTEX,{"derivedFrom":[subQ1,subQ0]});Q3=makeQuery(id+"F0.imprint","IMPRINT",FACE,{"disambiguationData":[TD([[makeQuery(id+"F0.imprint","IMPRINT",EDGE,{"disambiguationData":[TD([[subQ2,-1.0]])],"derivedFrom":subQ1}),1.0]])]});}
            var Q4;
            {var subQ0=sQuery(id+"F0.wireOp",EDGE,"E6.0");var subQ1=sQuery(id+"F0.wireOp",EDGE,"E1.left");var subQ2=makeQuery(id+"F0.imprint","INTERSECT",VERTEX,{"derivedFrom":[subQ1,subQ0]});Q4=makeQuery(id+"F0.imprint","IMPRINT",FACE,{"disambiguationData":[TD([[makeQuery(id+"F0.imprint","IMPRINT",EDGE,{"disambiguationData":[TD([[subQ2,1.0]])],"derivedFrom":subQ1}),1.0]])]});}
            extrude(context, id + "F29", {"entities" : qUnion([Q0, Q1, Q2, Q3, Q4]), "depth" : 25.4 * mm, "offsetDistance" : 25.4 * mm});
        }
        {
            var Q0;
            {var subQ0=sQuery(id+"F0.wireOp",EDGE,"E13.0");var subQ1=sQuery(id+"F0.wireOp",EDGE,"E2.0");var subQ2=makeQuery(id+"F0.imprint","INTERSECT",VERTEX,{"derivedFrom":[subQ1,subQ0]});Q0=makeQuery(id+"F0.imprint","IMPRINT",FACE,{"disambiguationData":[TD([[makeQuery(id+"F0.imprint","IMPRINT",EDGE,{"disambiguationData":[TD([[subQ2,-1.0]])],"derivedFrom":subQ1}),1.0]])]});}
            var Q1;
            {var subQ0=sQuery(id+"F0.wireOp",EDGE,"E14.0");var subQ1=sQuery(id+"F0.wireOp",EDGE,"E3.0");var subQ2=makeQuery(id+"F0.imprint","INTERSECT",VERTEX,{"derivedFrom":[subQ1,subQ0]});Q1=makeQuery(id+"F0.imprint","IMPRINT",FACE,{"disambiguationData":[TD([[makeQuery(id+"F0.imprint","IMPRINT",EDGE,{"disambiguationData":[TD([[subQ2,-1.0]])],"derivedFrom":subQ1}),1.0]])]});}
            var Q2;
            {var subQ0=sQuery(id+"F0.wireOp",EDGE,"E15.0");var subQ1=sQuery(id+"F0.wireOp",EDGE,"E4.0");var subQ2=makeQuery(id+"F0.imprint","INTERSECT",VERTEX,{"derivedFrom":[subQ1,subQ0]});Q2=makeQuery(id+"F0.imprint","IMPRINT",FACE,{"disambiguationData":[TD([[makeQuery(id+"F0.imprint","IMPRINT",EDGE,{"disambiguationData":[TD([[subQ2,-1.0]])],"derivedFrom":subQ1}),1.0]])]});}
            var Q3;
            {var subQ0=sQuery(id+"F0.wireOp",EDGE,"E5.0");var subQ1=sQuery(id+"F0.wireOp",EDGE,"E1.left");var subQ2=makeQuery(id+"F0.imprint","INTERSECT",VERTEX,{"derivedFrom":[subQ1,subQ0]});Q3=makeQuery(id+"F0.imprint","IMPRINT",FACE,{"disambiguationData":[TD([[makeQuery(id+"F0.imprint","IMPRINT",EDGE,{"disambiguationData":[TD([[subQ2,1.0]])],"derivedFrom":subQ1}),1.0]])]});}
            extrude(context, id + "F30", {"entities" : qUnion([Q0, Q1, Q2, Q3]), "depth" : 25.4 * mm, "offsetDistance" : 25.4 * mm});
        }
        {
            var Q0;
            {var subQ0=sQuery(id+"F0.wireOp",EDGE,"E14.0");var subQ1=sQuery(id+"F0.wireOp",EDGE,"E2.0");var subQ2=makeQuery(id+"F0.imprint","INTERSECT",VERTEX,{"derivedFrom":[subQ1,subQ0]});Q0=makeQuery(id+"F0.imprint","IMPRINT",FACE,{"disambiguationData":[TD([[makeQuery(id+"F0.imprint","IMPRINT",EDGE,{"disambiguationData":[TD([[subQ2,-1.0]])],"derivedFrom":subQ1}),1.0]])]});}
            var Q1;
            {var subQ0=sQuery(id+"F0.wireOp",EDGE,"E15.0");var subQ1=sQuery(id+"F0.wireOp",EDGE,"E3.0");var subQ2=makeQuery(id+"F0.imprint","INTERSECT",VERTEX,{"derivedFrom":[subQ1,subQ0]});Q1=makeQuery(id+"F0.imprint","IMPRINT",FACE,{"disambiguationData":[TD([[makeQuery(id+"F0.imprint","IMPRINT",EDGE,{"disambiguationData":[TD([[subQ2,-1.0]])],"derivedFrom":subQ1}),1.0]])]});}
            var Q2;
            {var subQ0=sQuery(id+"F0.wireOp",EDGE,"E4.0");var subQ1=sQuery(id+"F0.wireOp",EDGE,"E1.left");var subQ2=makeQuery(id+"F0.imprint","INTERSECT",VERTEX,{"derivedFrom":[subQ1,subQ0]});Q2=makeQuery(id+"F0.imprint","IMPRINT",FACE,{"disambiguationData":[TD([[makeQuery(id+"F0.imprint","IMPRINT",EDGE,{"disambiguationData":[TD([[subQ2,1.0]])],"derivedFrom":subQ1}),1.0]])]});}
            extrude(context, id + "F31", {"entities" : qUnion([Q0, Q1, Q2]), "depth" : 25.4 * mm, "offsetDistance" : 25.4 * mm});
        }
        {
            var Q0;
            {var subQ0=sQuery(id+"F0.wireOp",EDGE,"E15.0");var subQ1=sQuery(id+"F0.wireOp",EDGE,"E2.0");var subQ2=makeQuery(id+"F0.imprint","INTERSECT",VERTEX,{"derivedFrom":[subQ1,subQ0]});Q0=makeQuery(id+"F0.imprint","IMPRINT",FACE,{"disambiguationData":[TD([[makeQuery(id+"F0.imprint","IMPRINT",EDGE,{"disambiguationData":[TD([[subQ2,-1.0]])],"derivedFrom":subQ1}),1.0]])]});}
            var Q1;
            {var subQ0=sQuery(id+"F0.wireOp",EDGE,"E3.0");var subQ1=sQuery(id+"F0.wireOp",EDGE,"E1.left");var subQ2=makeQuery(id+"F0.imprint","INTERSECT",VERTEX,{"derivedFrom":[subQ1,subQ0]});Q1=makeQuery(id+"F0.imprint","IMPRINT",FACE,{"disambiguationData":[TD([[makeQuery(id+"F0.imprint","IMPRINT",EDGE,{"disambiguationData":[TD([[subQ2,1.0]])],"derivedFrom":subQ1}),1.0]])]});}
            extrude(context, id + "F32", {"entities" : qUnion([Q0, Q1]), "depth" : 25.4 * mm, "offsetDistance" : 25.4 * mm});
        }
        {
            var Q0;
            {var subQ0=sQuery(id+"F0.wireOp",EDGE,"E2.0");var subQ1=sQuery(id+"F0.wireOp",EDGE,"E1.left");var subQ2=makeQuery(id+"F0.imprint","INTERSECT",VERTEX,{"derivedFrom":[subQ1,subQ0]});Q0=makeQuery(id+"F0.imprint","IMPRINT",FACE,{"disambiguationData":[TD([[makeQuery(id+"F0.imprint","IMPRINT",EDGE,{"disambiguationData":[TD([[subQ2,1.0]])],"derivedFrom":subQ1}),1.0]])]});}
            extrude(context, id + "F33", {"entities" : qUnion([Q0]), "depth" : 25.4 * mm, "offsetDistance" : 25.4 * mm});
        }
    });
